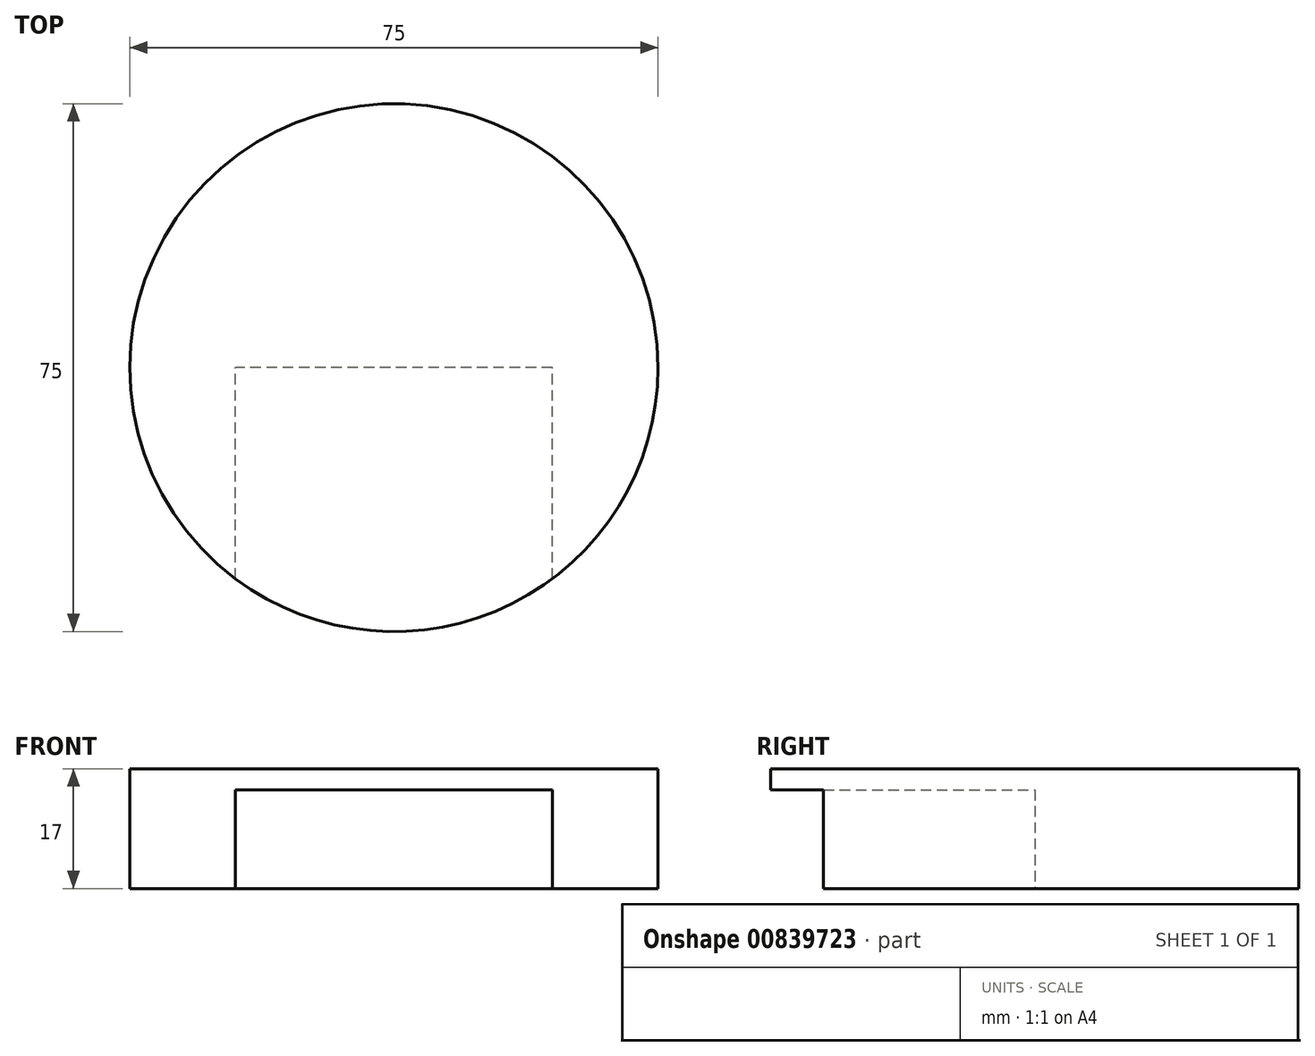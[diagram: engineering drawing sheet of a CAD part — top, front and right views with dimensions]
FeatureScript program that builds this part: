
annotation { "Feature Type Name" : "Feature", "Feature Type Description" : "" }
export const myFeature = defineFeature(function(context is Context, id is Id, definition is map)
    precondition{}
    {
        {
            var Q0;
            Q0=qCreatedBy(makeId("Top.planeOp"),FACE);
            var sketch = newSketch(context, id + "F0", { "sketchPlane" : qUnion([Q0])});
            skCircle(sketch, "E0", {"center": v(0, 0) * mm, "radius": 37.5 * mm});
            skLineSegment(sketch, "E1.bottom", {"start": v(22.5, -70) * mm, "end": v(-22.5, -70) * mm});
            skLineSegment(sketch, "E1.top", {"start": v(22.5, 0) * mm, "end": v(-22.5, 0) * mm});
            skLineSegment(sketch, "E1.left", {"start": v(22.5, -70) * mm, "end": v(22.5, 0) * mm});
            skLineSegment(sketch, "E1.right", {"start": v(-22.5, -70) * mm, "end": v(-22.5, 0) * mm});
            skSolve(sketch);
        }
        {
            var Q0;
            {var subQ5=sQuery(id+"F0.wireOp",EDGE,"E1.top");Q0=makeQuery(id+"F0.imprint","IMPRINT",FACE,{"disambiguationData":[TD([[makeQuery(id+"F0.imprint","IMPRINT",EDGE,{"derivedFrom":subQ5}),-1.0]])]});}
            var Q1;
            {var subQ5=sQuery(id+"F0.wireOp",EDGE,"E1.top");Q1=makeQuery(id+"F0.imprint","IMPRINT",FACE,{"disambiguationData":[TD([[makeQuery(id+"F0.imprint","IMPRINT",EDGE,{"derivedFrom":subQ5}),1.0]])]});}
            extrude(context, id + "F1", {"entities" : qUnion([Q0, Q1]), "depth" : 17 * mm, "offsetDistance" : 25 * mm});
        }
        {
            var Q0;
            {var subQ5=sQuery(id+"F0.wireOp",EDGE,"E1.top");Q0=makeQuery(id+"F0.imprint","IMPRINT",FACE,{"disambiguationData":[TD([[makeQuery(id+"F0.imprint","IMPRINT",EDGE,{"derivedFrom":subQ5}),1.0]])]});}
            var Q1;
            {var subQ5=sQuery(id+"F0.wireOp",EDGE,"E1.bottom");Q1=makeQuery(id+"F0.imprint","IMPRINT",FACE,{"disambiguationData":[TD([[makeQuery(id+"F0.imprint","IMPRINT",EDGE,{"derivedFrom":subQ5}),-1.0]])]});}
            extrude(context, id + "F2", {"entities" : qUnion([Q0, Q1]), "operationType" : NewBodyOperationType.REMOVE, "depth" : 14 * mm, "offsetDistance" : 25 * mm});
        }
    });
